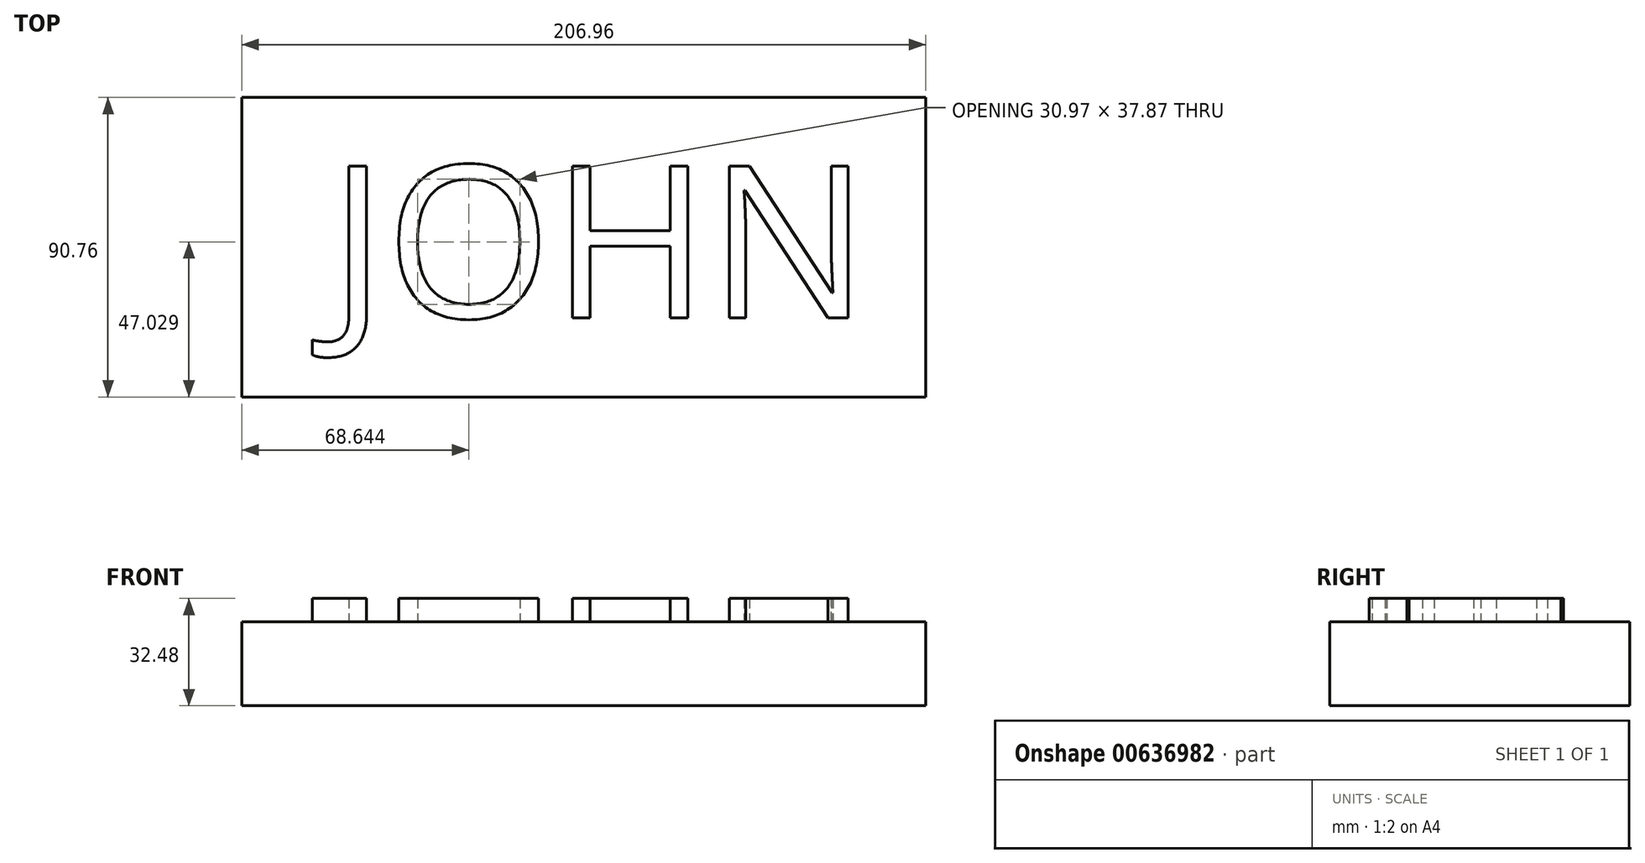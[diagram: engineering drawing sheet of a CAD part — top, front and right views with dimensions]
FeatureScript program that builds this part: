
annotation { "Feature Type Name" : "Feature", "Feature Type Description" : "" }
export const myFeature = defineFeature(function(context is Context, id is Id, definition is map)
    precondition{}
    {
        {
            var Q0;
            Q0=qCreatedBy(makeId("Top.planeOp"),FACE);
            var sketch = newSketch(context, id + "F0", { "sketchPlane" : qUnion([Q0])});
            skText(sketch, "E0", { "text": "JOHN", "fontName": "OpenSans-Regular.ttf"});
            const initialGuessF0  = {"E0": [0, 0, 1, 0, 0.04637]};
            skSetInitialGuess(sketch, initialGuessF0);
            skSolve(sketch);
        }
        {
            var Q0;
            Q0=makeQuery(id+"F0.imprint","IMPRINT",FACE,{"disambiguationData":[TD([[makeQuery(id+"F0.imprint","IMPRINT",EDGE,{"derivedFrom":sQuery(id+"F0.wireOp",EDGE,"E0.sketch_text.stroke-0")}),-1.0]])]});
            var Q1;
            Q1=makeQuery(id+"F0.imprint","IMPRINT",FACE,{"disambiguationData":[TD([[makeQuery(id+"F0.imprint","IMPRINT",EDGE,{"derivedFrom":sQuery(id+"F0.wireOp",EDGE,"E0.sketch_text.stroke-10")}),-1.0]])]});
            var Q2;
            Q2=makeQuery(id+"F0.imprint","IMPRINT",FACE,{"disambiguationData":[TD([[makeQuery(id+"F0.imprint","IMPRINT",EDGE,{"derivedFrom":sQuery(id+"F0.wireOp",EDGE,"E0.sketch_text.stroke-26")}),-1.0]])]});
            var Q3;
            Q3=makeQuery(id+"F0.imprint","IMPRINT",FACE,{"disambiguationData":[TD([[makeQuery(id+"F0.imprint","IMPRINT",EDGE,{"derivedFrom":sQuery(id+"F0.wireOp",EDGE,"E0.sketch_text.stroke-38")}),-1.0]])]});
            extrude(context, id + "F1", {"entities" : qUnion([Q0, Q1, Q2, Q3]), "depth" : 7.08 * mm, "offsetDistance" : 25.4 * mm});
        }
        {
            var Q0;
            Q0=qCreatedBy(makeId("Top.planeOp"),FACE);
            var sketch = newSketch(context, id + "F2", { "sketchPlane" : qUnion([Q0])});
            skLineSegment(sketch, "E1.bottom", {"start": v(-26.37, -24.04) * mm, "end": v(180.6, -24.04) * mm});
            skLineSegment(sketch, "E1.top", {"start": v(-26.37, 66.72) * mm, "end": v(180.6, 66.72) * mm});
            skLineSegment(sketch, "E1.left", {"start": v(-26.37, -24.04) * mm, "end": v(-26.37, 66.72) * mm});
            skLineSegment(sketch, "E1.right", {"start": v(180.6, -24.04) * mm, "end": v(180.6, 66.72) * mm});
            skPoint(sketch, "E1.middle", {"position": v(77.11, 21.34) * mm});
            skSolve(sketch);
        }
        {
            var Q0;
            Q0=makeQuery(id+"F2.imprint","IMPRINT",FACE,{"disambiguationData":[TD([[makeQuery(id+"F2.imprint","IMPRINT",EDGE,{"derivedFrom":sQuery(id+"F2.wireOp",EDGE,"E1.bottom")}),1.0]])]});
            extrude(context, id + "F3", {"entities" : qUnion([Q0]), "depth" : -25.4 * mm, "offsetDistance" : 25.4 * mm});
        }
    });
